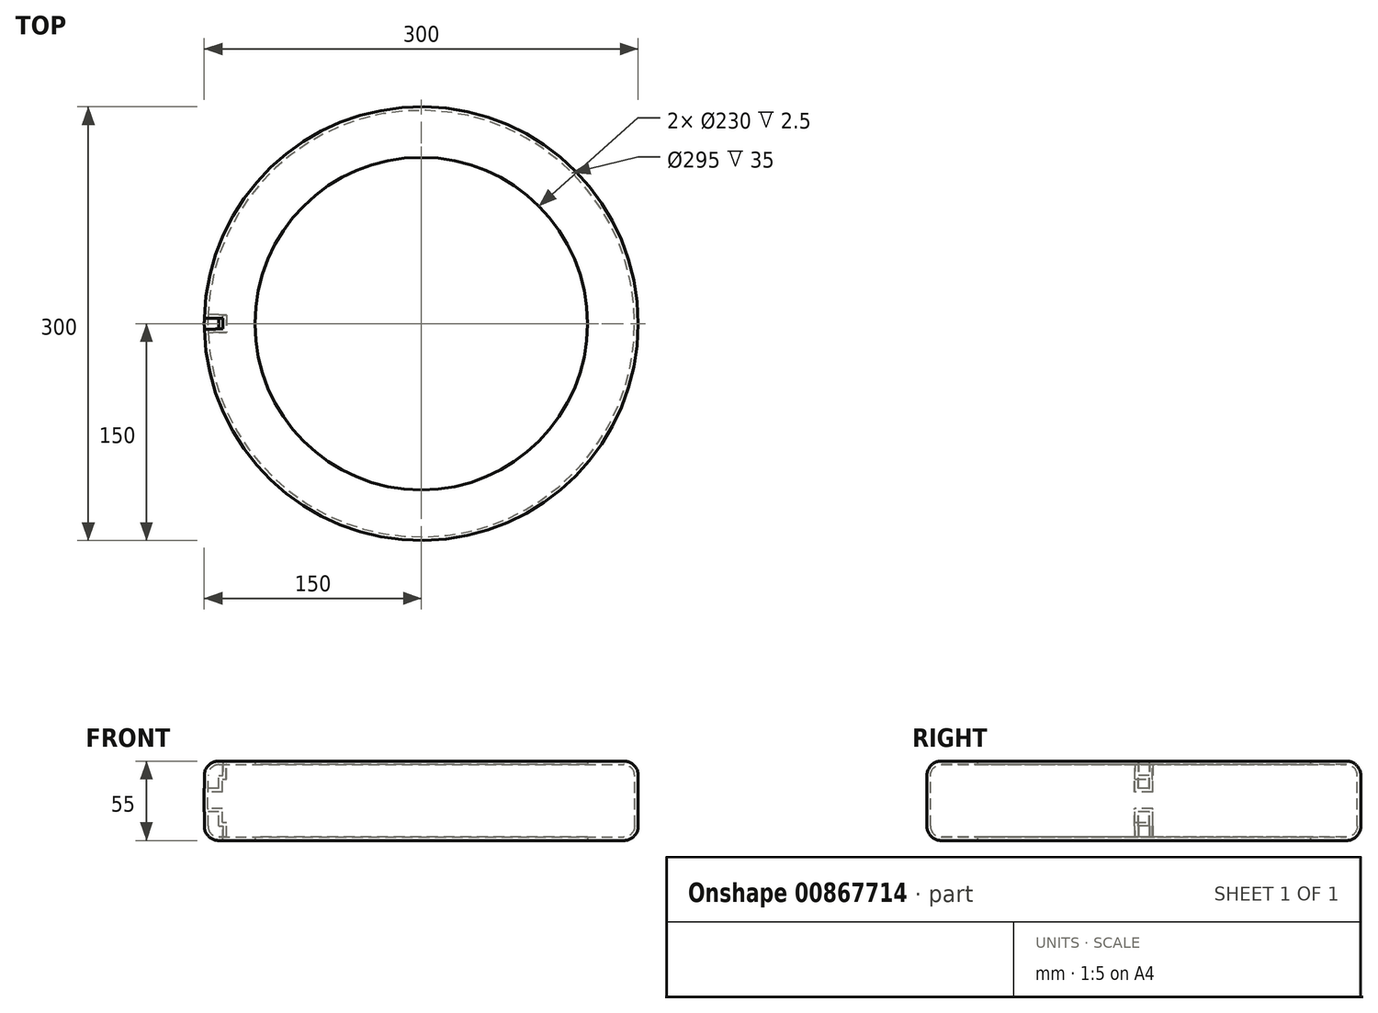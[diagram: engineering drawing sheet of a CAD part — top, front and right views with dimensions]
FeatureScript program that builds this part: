
annotation { "Feature Type Name" : "Feature", "Feature Type Description" : "" }
export const myFeature = defineFeature(function(context is Context, id is Id, definition is map)
    precondition{}
    {
        {
            var Q0;
            Q0=qCreatedBy(makeId("Front.planeOp"),FACE);
            var sketch = newSketch(context, id + "F0", { "sketchPlane" : qUnion([Q0])});
            skLineSegment(sketch, "E0.bottom", {"start": v(0, 0) * mm, "end": v(-150, 0) * mm});
            skLineSegment(sketch, "E0.top", {"start": v(0, 55) * mm, "end": v(-150, 55) * mm});
            skLineSegment(sketch, "E0.left", {"start": v(0, 0) * mm, "end": v(0, 55) * mm});
            skLineSegment(sketch, "E0.right", {"start": v(-150, 0) * mm, "end": v(-150, 55) * mm});
            skLineSegment(sketch, "E1", {"start": v(0, 72.43) * mm, "end": v(0, -50.14) * mm});
            skSolve(sketch);
        }
        {
            var Q0;
            Q0=qSketchRegion(id+"F0",true);
            var Q1;
            Q1=sQuery(id+"F0.wireOp",EDGE,"E1");
            revolve(context, id + "F1", {"surfaceOperationType" : NewSurfaceOperationType.NEW, "entities" : qUnion([Q0]), "axis" : qUnion([Q1]), "revolveType" : RevolveType.FULL});
        }
        {
            var Q0;
            Q0=makeQuery(id+"F1.opRevolve","SWEPT_EDGE",EDGE,{"disambiguationData":[OSD([sQuery(id+"F0.wireOp",EDGE,"E0.top"),sQuery(id+"F0.wireOp",EDGE,"E0.right")])]});
            var Q1;
            Q1=makeQuery(id+"F1.opRevolve","SWEPT_FACE",FACE,{"disambiguationData":[OSD([sQuery(id+"F0.wireOp",EDGE,"E0.bottom")])]});
            fillet(context, id + "F2", {"entities" : qUnion([Q0, Q1]), "radius" : 10 * mm, "tangentPropagation" : true, "allowEdgeOverflow" : false});
        }
        {
            var Q0;
            Q0=qCreatedBy(makeId("Front.planeOp"),FACE);
            var sketch = newSketch(context, id + "F3", { "sketchPlane" : qUnion([Q0])});
            skLineSegment(sketch, "E2", {"start": v(150, 45) * mm, "end": v(150, 13.16) * mm});
            skLineSegment(sketch, "E3", {"start": v(-150, 10) * mm, "end": v(-150, 45.04) * mm});
            skLineSegment(sketch, "E4", {"start": v(-140, 55) * mm, "end": v(140, 55) * mm});
            skArc(sketch, "E5", {"start": v(-140, 55) * mm, "mid": v(-147.07, 52.07) * mm, "end": v(-150, 45) * mm});
            skArc(sketch, "E6", {"start": v(150, 45) * mm, "mid": v(147.07, 52.07) * mm, "end": v(140, 55) * mm});
            skLineSegment(sketch, "E7.0", {"start": v(-140, 45) * mm, "end": v(140, 45) * mm});
            skLineSegment(sketch, "E8.0", {"start": v(-140, 45) * mm, "end": v(-140, 45) * mm});
            skLineSegment(sketch, "E9.0", {"start": v(-140, 10) * mm, "end": v(-140, 45) * mm});
            skLineSegment(sketch, "E10.0", {"start": v(140, 45) * mm, "end": v(140, 45) * mm});
            skLineSegment(sketch, "E11.0", {"start": v(140, 45) * mm, "end": v(140, 10) * mm});
            skLineSegment(sketch, "E12", {"start": v(-137.28, 55) * mm, "end": v(-137.28, 45) * mm});
            skLineSegment(sketch, "E13", {"start": v(-140, 36.04) * mm, "end": v(-150, 36.04) * mm});
            skLineSegment(sketch, "E14", {"start": v(0, -51.78) * mm, "end": v(0, 108.92) * mm});
            skLineSegment(sketch, "E15", {"start": v(-140, 0) * mm, "end": v(140, 0) * mm});
            skArc(sketch, "E16", {"start": v(-150, 10) * mm, "mid": v(-147.07, 2.93) * mm, "end": v(-140, 0) * mm});
            skArc(sketch, "E17", {"start": v(140, 0) * mm, "mid": v(147.07, 2.93) * mm, "end": v(150, 10) * mm});
            skLineSegment(sketch, "E18.0", {"start": v(-150, 10) * mm, "end": v(150, 10) * mm});
            skLineSegment(sketch, "E19", {"start": v(140, 22.16) * mm, "end": v(150, 22.16) * mm});
            skLineSegment(sketch, "E20", {"start": v(137.63, 10) * mm, "end": v(137.63, 0) * mm});
            skLineSegment(sketch, "E21", {"start": v(-140, 19.47) * mm, "end": v(-150, 19.47) * mm});
            skLineSegment(sketch, "E22", {"start": v(-137.8, 10) * mm, "end": v(-137.8, 0) * mm});
            skSolve(sketch);
        }
        {
            var Q0;
            {var subQ4=sQuery(id+"F3.wireOp",EDGE,"E5");Q0=makeQuery(id+"F3.imprint","IMPRINT",FACE,{"disambiguationData":[TD([[makeQuery(id+"F3.imprint","IMPRINT",EDGE,{"derivedFrom":subQ4}),1.0]])]});}
            var Q1;
            Q1=sQuery(id+"F3.wireOp",EDGE,"E14");
            revolve(context, id + "F4", {"operationType" : NewBodyOperationType.REMOVE, "surfaceOperationType" : NewSurfaceOperationType.NEW, "entities" : qUnion([Q0]), "axis" : qUnion([Q1]), "revolveType" : RevolveType.SYMMETRIC, "oppositeDirection" : true, "angle" : 3 * degree});
        }
        {
            var Q0;
            Q0=qCreatedBy(makeId("Front.planeOp"),FACE);
            var sketch = newSketch(context, id + "F5", { "sketchPlane" : qUnion([Q0])});
            skLineSegment(sketch, "E23.0", {"start": v(0, 0) * mm, "end": v(-150, 0) * mm});
            skArc(sketch, "E24", {"start": v(-150, 10) * mm, "mid": v(-147.07, 2.93) * mm, "end": v(-140, 0) * mm});
            skLineSegment(sketch, "E25", {"start": v(-150, 10) * mm, "end": v(-150, 36.04) * mm});
            skLineSegment(sketch, "E26.0", {"start": v(-140, 10) * mm, "end": v(-140, 10) * mm});
            skLineSegment(sketch, "E27.0", {"start": v(-140, 10) * mm, "end": v(-140, 36.04) * mm});
            skLineSegment(sketch, "E28", {"start": v(-140, 10) * mm, "end": v(-43.5, 10) * mm});
            skLineSegment(sketch, "E29", {"start": v(-140, 19.78) * mm, "end": v(-150, 19.78) * mm});
            skLineSegment(sketch, "E30", {"start": v(-137.23, 10) * mm, "end": v(-137.23, 0) * mm});
            skSolve(sketch);
        }
        {
            var Q0;
            Q0=qSketchRegion(id+"F5",true);
            var Q1;
            Q1=sQuery(id+"F0.wireOp",EDGE,"E1");
            revolve(context, id + "F6", {"operationType" : NewBodyOperationType.REMOVE, "surfaceOperationType" : NewSurfaceOperationType.NEW, "entities" : qUnion([Q0]), "axis" : qUnion([Q1]), "revolveType" : RevolveType.SYMMETRIC, "angle" : 3 * degree});
        }
        {
            var Q0;
            Q0=qCreatedBy(makeId("Top.planeOp"),FACE);
            cPlane(context, id + "F7", {"entities" : qUnion([Q0]), "cplaneType" : CPlaneType.OFFSET, "offset" : 5 * mm, "width" : 150 * mm, "height" : 150 * mm});
        }
        {
            var Q0;
            Q0=qCreatedBy(makeId("Top.planeOp"),FACE);
            var sketch = newSketch(context, id + "F8", { "sketchPlane" : qUnion([Q0])});
            skCircle(sketch, "E31", {"center": v(0, 0) * mm, "radius": 45.81 * mm});
            skCircle(sketch, "E32", {"center": v(0, 0) * mm, "radius": 115 * mm});
            skSolve(sketch);
        }
        {
            var Q0;
            Q0=qSketchRegion(id+"F8",true);
            extrude(context, id + "F9", {"entities" : qUnion([Q0]), "operationType" : NewBodyOperationType.REMOVE, "depth" : 100 * mm, "offsetDistance" : 25 * mm});
        }
        {
            var Q0;
            Q0=makeQuery(id+"F8.imprint","IMPRINT",FACE,{"disambiguationData":[TD([[makeQuery(id+"F8.imprint","IMPRINT",EDGE,{"derivedFrom":sQuery(id+"F8.wireOp",EDGE,"E31")}),1.0]])]});
            extrude(context, id + "F10", {"entities" : qUnion([Q0]), "operationType" : NewBodyOperationType.REMOVE, "depth" : 100 * mm, "offsetDistance" : 25 * mm});
        }
        {
            var Q0;
            Q0=makeQuery(id+"F9.boolean.opBoolean","COPY",FACE,{"derivedFrom":makeQuery(id+"F9.opExtrude","SWEPT_FACE",FACE,{"disambiguationData":[OSD([sQuery(id+"F8.wireOp",EDGE,"E32")])]})});
            shell(context, id + "F11", {"entities" : qUnion([Q0]), "thickness" : 2.5 * mm});
        }
    });
